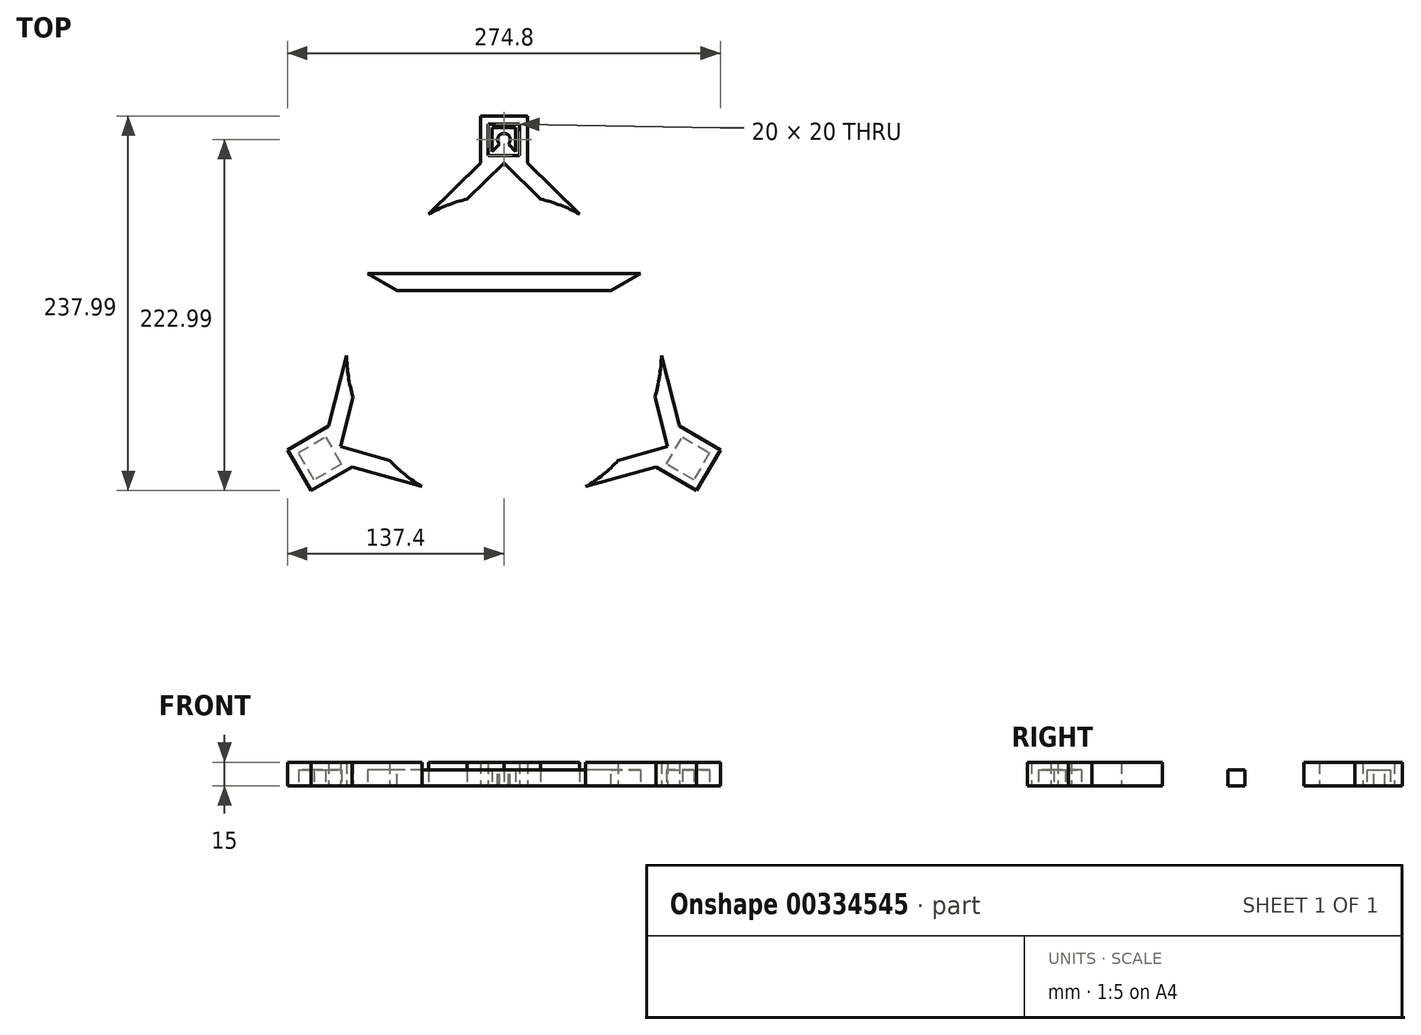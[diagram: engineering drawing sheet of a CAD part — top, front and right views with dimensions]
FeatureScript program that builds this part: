
annotation { "Feature Type Name" : "Feature", "Feature Type Description" : "" }
export const myFeature = defineFeature(function(context is Context, id is Id, definition is map)
    precondition{}
    {
        {
            var Q0;
            Q0=qCreatedBy(makeId("Top.planeOp"),FACE);
            var sketch = newSketch(context, id + "F0", { "sketchPlane" : qUnion([Q0])});
            skCircle(sketch, "E0", {"center": v(0, 0) * mm, "radius": 100 * mm});
            skLineSegment(sketch, "E1", {"start": v(0, 0) * mm, "end": v(0, -100) * mm});
            skLineSegment(sketch, "E2", {"start": v(0, 0) * mm, "end": v(86.6, 50) * mm});
            skLineSegment(sketch, "E3", {"start": v(0, 0) * mm, "end": v(-86.6, 50) * mm});
            skLineSegment(sketch, "E4", {"start": v(-86.6, 50) * mm, "end": v(0, -100) * mm});
            skLineSegment(sketch, "E5", {"start": v(0, -100) * mm, "end": v(86.6, 50) * mm});
            skLineSegment(sketch, "E6", {"start": v(86.6, 50) * mm, "end": v(-86.6, 50) * mm});
            skLineSegment(sketch, "E7", {"start": v(0, 0) * mm, "end": v(0, 125) * mm});
            skPoint(sketch, "E7.endSnap0", {"position": v(0, 50) * mm});
            skLineSegment(sketch, "E8", {"start": v(0, 0) * mm, "end": v(108.25, -62.5) * mm});
            skLineSegment(sketch, "E9", {"start": v(0, 0) * mm, "end": v(-108.25, -62.5) * mm});
            skLineSegment(sketch, "E10", {"start": v(-108.25, -62.5) * mm, "end": v(-113.25, -53.84) * mm});
            skLineSegment(sketch, "E11", {"start": v(-108.25, -62.5) * mm, "end": v(-103.25, -71.16) * mm});
            skLineSegment(sketch, "E12", {"start": v(-103.25, -71.16) * mm, "end": v(-120.57, -81.16) * mm});
            skLineSegment(sketch, "E13", {"start": v(-120.57, -81.16) * mm, "end": v(-130.57, -63.84) * mm});
            skLineSegment(sketch, "E14", {"start": v(-130.57, -63.84) * mm, "end": v(-113.25, -53.84) * mm});
            skLineSegment(sketch, "E15", {"start": v(0, 125) * mm, "end": v(10, 125) * mm});
            skLineSegment(sketch, "E16", {"start": v(10, 125) * mm, "end": v(10, 145) * mm});
            skLineSegment(sketch, "E17", {"start": v(10, 145) * mm, "end": v(-10, 145) * mm});
            skLineSegment(sketch, "E18", {"start": v(-10, 145) * mm, "end": v(-10, 125) * mm});
            skLineSegment(sketch, "E19", {"start": v(-10, 125) * mm, "end": v(0, 125) * mm});
            skLineSegment(sketch, "E20", {"start": v(108.25, -62.5) * mm, "end": v(113.25, -53.84) * mm});
            skLineSegment(sketch, "E21", {"start": v(113.25, -53.84) * mm, "end": v(130.57, -63.84) * mm});
            skLineSegment(sketch, "E22", {"start": v(130.57, -63.84) * mm, "end": v(120.57, -81.16) * mm});
            skLineSegment(sketch, "E23", {"start": v(120.57, -81.16) * mm, "end": v(103.25, -71.16) * mm});
            skLineSegment(sketch, "E24", {"start": v(103.25, -71.16) * mm, "end": v(108.25, -62.5) * mm});
            skLineSegment(sketch, "E25", {"start": v(-120.57, -81.16) * mm, "end": v(-113.25, -53.84) * mm});
            skLineSegment(sketch, "E26", {"start": v(-103.25, -71.16) * mm, "end": v(-130.57, -63.84) * mm});
            skLineSegment(sketch, "E27", {"start": v(113.25, -53.84) * mm, "end": v(120.57, -81.16) * mm});
            skLineSegment(sketch, "E28", {"start": v(103.25, -71.16) * mm, "end": v(130.57, -63.84) * mm});
            skLineSegment(sketch, "E29", {"start": v(-10, 145) * mm, "end": v(7.5, 127.5) * mm});
            skLineSegment(sketch, "E30", {"start": v(-7.5, 127.5) * mm, "end": v(10, 145) * mm});
            skLineSegment(sketch, "E31.bottom", {"start": v(15, 120) * mm, "end": v(-15, 120) * mm});
            skLineSegment(sketch, "E31.top", {"start": v(15, 150) * mm, "end": v(-15, 150) * mm});
            skLineSegment(sketch, "E31.left", {"start": v(15, 120) * mm, "end": v(15, 150) * mm});
            skLineSegment(sketch, "E31.right", {"start": v(-15, 120) * mm, "end": v(-15, 150) * mm});
            skPoint(sketch, "E31.middle", {"position": v(0, 135) * mm});
            skLineSegment(sketch, "E32", {"start": v(-15, 120) * mm, "end": v(-86.6, 50) * mm});
            skLineSegment(sketch, "E33", {"start": v(-86.6, 50) * mm, "end": v(-71.6, 50) * mm});
            skLineSegment(sketch, "E34", {"start": v(-71.6, 50) * mm, "end": v(0, 120) * mm});
            skLineSegment(sketch, "E35", {"start": v(86.6, 50) * mm, "end": v(71.6, 50) * mm});
            skLineSegment(sketch, "E36", {"start": v(71.6, 50) * mm, "end": v(0, 120) * mm});
            skLineSegment(sketch, "E37", {"start": v(15, 120) * mm, "end": v(86.6, 50) * mm});
            skLineSegment(sketch, "E38.bottom", {"start": v(-10, 125) * mm, "end": v(10, 125) * mm});
            skLineSegment(sketch, "E38.top", {"start": v(-10, 127.5) * mm, "end": v(10, 127.5) * mm});
            skLineSegment(sketch, "E38.left", {"start": v(-10, 125) * mm, "end": v(-10, 127.5) * mm});
            skLineSegment(sketch, "E38.right", {"start": v(10, 125) * mm, "end": v(10, 127.5) * mm});
            skLineSegment(sketch, "E39.bottom", {"start": v(7.5, 127.5) * mm, "end": v(-7.5, 127.5) * mm});
            skLineSegment(sketch, "E39.top", {"start": v(7.5, 142.5) * mm, "end": v(-7.5, 142.5) * mm});
            skLineSegment(sketch, "E39.left", {"start": v(7.5, 127.5) * mm, "end": v(7.5, 142.5) * mm});
            skLineSegment(sketch, "E39.right", {"start": v(-7.5, 127.5) * mm, "end": v(-7.5, 142.5) * mm});
            skSolve(sketch);
        }
        {
            var Q0;
            {var subQ5=sQuery(id+"F0.wireOp",EDGE,"E33");Q0=makeQuery(id+"F0.imprint","IMPRINT",FACE,{"disambiguationData":[TD([[makeQuery(id+"F0.imprint","IMPRINT",EDGE,{"derivedFrom":subQ5}),1.0]])]});}
            var Q1;
            {var subQ0=sQuery(id+"F0.wireOp",EDGE,"E32");var subQ1=sQuery(id+"F0.wireOp",EDGE,"E0");var subQ2=makeQuery(id+"F0.imprint","INTERSECT",VERTEX,{"derivedFrom":[subQ1,subQ0]});Q1=makeQuery(id+"F0.imprint","IMPRINT",FACE,{"disambiguationData":[TD([[makeQuery(id+"F0.imprint","IMPRINT",EDGE,{"disambiguationData":[TD([[subQ2,1.0]])],"derivedFrom":subQ1}),-1.0]])]});}
            var Q2;
            {var subQ0=sQuery(id+"F0.wireOp",EDGE,"E37");var subQ1=sQuery(id+"F0.wireOp",EDGE,"E0");var subQ2=makeQuery(id+"F0.imprint","INTERSECT",VERTEX,{"derivedFrom":[subQ1,subQ0]});Q2=makeQuery(id+"F0.imprint","IMPRINT",FACE,{"disambiguationData":[TD([[makeQuery(id+"F0.imprint","IMPRINT",EDGE,{"disambiguationData":[TD([[subQ2,-1.0]])],"derivedFrom":subQ1}),-1.0]])]});}
            var Q3;
            {var subQ5=sQuery(id+"F0.wireOp",EDGE,"E35");Q3=makeQuery(id+"F0.imprint","IMPRINT",FACE,{"disambiguationData":[TD([[makeQuery(id+"F0.imprint","IMPRINT",EDGE,{"derivedFrom":subQ5}),-1.0]])]});}
            var Q4;
            Q4=makeQuery(id+"F0.imprint","IMPRINT",FACE,{"disambiguationData":[TD([[makeQuery(id+"F0.imprint","IMPRINT",EDGE,{"derivedFrom":sQuery(id+"F0.wireOp",EDGE,"E15")}),-1.0]])]});
            var Q5;
            {var subQ0=sQuery(id+"F0.wireOp",EDGE,"E3");Q5=makeQuery(id+"F0.imprint","IMPRINT",FACE,{"disambiguationData":[TD([[makeQuery(id+"F0.imprint","IMPRINT",EDGE,{"derivedFrom":subQ0}),-1.0]])]});}
            var Q6;
            {var subQ0=sQuery(id+"F0.wireOp",EDGE,"E2");Q6=makeQuery(id+"F0.imprint","IMPRINT",FACE,{"disambiguationData":[TD([[makeQuery(id+"F0.imprint","IMPRINT",EDGE,{"derivedFrom":subQ0}),1.0]])]});}
            var Q7;
            Q7=makeQuery(id+"F0.imprint","IMPRINT",FACE,{"disambiguationData":[TD([[makeQuery(id+"F0.imprint","IMPRINT",EDGE,{"derivedFrom":sQuery(id+"F0.wireOp",EDGE,"E16")}),-1.0]])]});
            var Q8;
            {var subQ3=sQuery(id+"F0.wireOp",EDGE,"E38.left");Q8=makeQuery(id+"F0.imprint","IMPRINT",FACE,{"disambiguationData":[TD([[makeQuery(id+"F0.imprint","IMPRINT",EDGE,{"derivedFrom":subQ3}),-1.0]])]});}
            var Q9;
            {var subQ0=sQuery(id+"F0.wireOp",EDGE,"E39.right");Q9=makeQuery(id+"F0.imprint","IMPRINT",FACE,{"disambiguationData":[TD([[makeQuery(id+"F0.imprint","IMPRINT",EDGE,{"derivedFrom":subQ0}),-1.0]])]});}
            var Q10;
            {var subQ0=sQuery(id+"F0.wireOp",EDGE,"E39.bottom");Q10=makeQuery(id+"F0.imprint","IMPRINT",FACE,{"disambiguationData":[TD([[makeQuery(id+"F0.imprint","IMPRINT",EDGE,{"derivedFrom":subQ0}),-1.0]])]});}
            var Q11;
            {var subQ0=sQuery(id+"F0.wireOp",EDGE,"E39.top");Q11=makeQuery(id+"F0.imprint","IMPRINT",FACE,{"disambiguationData":[TD([[makeQuery(id+"F0.imprint","IMPRINT",EDGE,{"derivedFrom":subQ0}),1.0]])]});}
            var Q12;
            {var subQ0=sQuery(id+"F0.wireOp",EDGE,"E39.left");Q12=makeQuery(id+"F0.imprint","IMPRINT",FACE,{"disambiguationData":[TD([[makeQuery(id+"F0.imprint","IMPRINT",EDGE,{"derivedFrom":subQ0}),1.0]])]});}
            extrude(context, id + "F1", {"entities" : qUnion([Q0, Q1, Q2, Q3, Q4, Q5, Q6, Q7, Q8, Q9, Q10, Q11, Q12]), "depth" : 10 * mm});
        }
        {
            var Q0;
            Q0=makeQuery(id+"F1.opExtrude","CAP_FACE",FACE,{"disambiguationData":[OSD([sQuery(id+"F0.wireOp",EDGE,"E2"),sQuery(id+"F0.wireOp",EDGE,"E3"),sQuery(id+"F0.wireOp",EDGE,"E6"),sQuery(id+"F0.wireOp",EDGE,"E16"),sQuery(id+"F0.wireOp",EDGE,"E17"),sQuery(id+"F0.wireOp",EDGE,"E18"),sQuery(id+"F0.wireOp",EDGE,"E31.top"),sQuery(id+"F0.wireOp",EDGE,"E31.left"),sQuery(id+"F0.wireOp",EDGE,"E31.right"),sQuery(id+"F0.wireOp",EDGE,"E32"),sQuery(id+"F0.wireOp",EDGE,"E34"),sQuery(id+"F0.wireOp",EDGE,"E36"),sQuery(id+"F0.wireOp",EDGE,"E37"),sQuery(id+"F0.wireOp",EDGE,"E38.top"),sQuery(id+"F0.wireOp",EDGE,"E39.top"),sQuery(id+"F0.wireOp",EDGE,"E39.left"),sQuery(id+"F0.wireOp",EDGE,"E39.right")])],"isStart":false});
            var sketch = newSketch(context, id + "F2", { "sketchPlane" : qUnion([Q0])});
            skLineSegment(sketch, "E40.bottom", {"start": v(-7.5, 142.5) * mm, "end": v(7.5, 142.5) * mm});
            skLineSegment(sketch, "E40.top", {"start": v(-7.5, 127.5) * mm, "end": v(7.5, 127.5) * mm});
            skLineSegment(sketch, "E40.left", {"start": v(-7.5, 142.5) * mm, "end": v(-7.5, 127.5) * mm});
            skLineSegment(sketch, "E40.right", {"start": v(7.5, 142.5) * mm, "end": v(7.5, 127.5) * mm});
            skCircle(sketch, "E41", {"center": v(0, 135) * mm, "radius": 4 * mm});
            skPoint(sketch, "E41.centerSnap0", {"position": v(-7.5, 135) * mm});
            skSolve(sketch);
        }
        {
            var Q0;
            Q0=makeQuery(id+"F2.imprint","IMPRINT",FACE,{"disambiguationData":[TD([[makeQuery(id+"F2.imprint","IMPRINT",EDGE,{"derivedFrom":sQuery(id+"F2.wireOp",EDGE,"E41")}),1.0]])]});
            extrude(context, id + "F3", {"entities" : qUnion([Q0]), "operationType" : NewBodyOperationType.REMOVE, "oppositeDirection" : true, "depth" : 25 * mm});
        }
        {
            var Q0;
            Q0=makeQuery(id+"F1.opExtrude","SWEPT_BODY",BODY,{"disambiguationData":[OSD([sQuery(id+"F0.wireOp",EDGE,"E2"),sQuery(id+"F0.wireOp",EDGE,"E3"),sQuery(id+"F0.wireOp",EDGE,"E6"),sQuery(id+"F0.wireOp",EDGE,"E15"),sQuery(id+"F0.wireOp",EDGE,"E16"),sQuery(id+"F0.wireOp",EDGE,"E17"),sQuery(id+"F0.wireOp",EDGE,"E18"),sQuery(id+"F0.wireOp",EDGE,"E19"),sQuery(id+"F0.wireOp",EDGE,"E31.top"),sQuery(id+"F0.wireOp",EDGE,"E31.left"),sQuery(id+"F0.wireOp",EDGE,"E31.right"),sQuery(id+"F0.wireOp",EDGE,"E32"),sQuery(id+"F0.wireOp",EDGE,"E34"),sQuery(id+"F0.wireOp",EDGE,"E36"),sQuery(id+"F0.wireOp",EDGE,"E37")])]});
            var Q1;
            Q1=makeQuery(id+"F1.opExtrude","SWEPT_FACE",FACE,{"disambiguationData":[OSD([sQuery(id+"F0.wireOp",EDGE,"E3")])]});
            mirror(context, id + "F4", {"entities" : qUnion([Q0]), "mirrorPlane" : qUnion([Q1])});
        }
        {
            var Q0;
            Q0=makeQuery(id+"F1.opExtrude","SWEPT_BODY",BODY,{"disambiguationData":[OSD([sQuery(id+"F0.wireOp",EDGE,"E2"),sQuery(id+"F0.wireOp",EDGE,"E3"),sQuery(id+"F0.wireOp",EDGE,"E6"),sQuery(id+"F0.wireOp",EDGE,"E15"),sQuery(id+"F0.wireOp",EDGE,"E16"),sQuery(id+"F0.wireOp",EDGE,"E17"),sQuery(id+"F0.wireOp",EDGE,"E18"),sQuery(id+"F0.wireOp",EDGE,"E19"),sQuery(id+"F0.wireOp",EDGE,"E31.top"),sQuery(id+"F0.wireOp",EDGE,"E31.left"),sQuery(id+"F0.wireOp",EDGE,"E31.right"),sQuery(id+"F0.wireOp",EDGE,"E32"),sQuery(id+"F0.wireOp",EDGE,"E34"),sQuery(id+"F0.wireOp",EDGE,"E36"),sQuery(id+"F0.wireOp",EDGE,"E37")])]});
            var Q1;
            Q1=makeQuery(id+"F1.opExtrude","SWEPT_FACE",FACE,{"disambiguationData":[OSD([sQuery(id+"F0.wireOp",EDGE,"E2")])]});
            mirror(context, id + "F5", {"operationType" : NewBodyOperationType.ADD, "entities" : qUnion([Q0]), "mirrorPlane" : qUnion([Q1])});
        }
        {
            var Q0;
            {var subQ0=makeQuery(id+"F1.opExtrude","CAP_FACE",FACE,{"disambiguationData":[OSD([sQuery(id+"F0.wireOp",EDGE,"E2"),sQuery(id+"F0.wireOp",EDGE,"E3"),sQuery(id+"F0.wireOp",EDGE,"E6"),sQuery(id+"F0.wireOp",EDGE,"E15"),sQuery(id+"F0.wireOp",EDGE,"E16"),sQuery(id+"F0.wireOp",EDGE,"E17"),sQuery(id+"F0.wireOp",EDGE,"E18"),sQuery(id+"F0.wireOp",EDGE,"E19"),sQuery(id+"F0.wireOp",EDGE,"E31.top"),sQuery(id+"F0.wireOp",EDGE,"E31.left"),sQuery(id+"F0.wireOp",EDGE,"E31.right"),sQuery(id+"F0.wireOp",EDGE,"E32"),sQuery(id+"F0.wireOp",EDGE,"E34"),sQuery(id+"F0.wireOp",EDGE,"E36"),sQuery(id+"F0.wireOp",EDGE,"E37")])],"isStart":false});Q0=makeQuery(id+"F5.boolean.opBoolean","MERGE",FACE,{"derivedFrom":[subQ0,makeQuery(id+"F4.opPattern","COPY",FACE,{"derivedFrom":subQ0,"instanceName":"1"}),makeQuery(id+"F5.opPattern","COPY",FACE,{"derivedFrom":subQ0,"instanceName":"1"})]});}
            var sketch = newSketch(context, id + "F6", { "sketchPlane" : qUnion([Q0])});
            skLineSegment(sketch, "E42", {"start": v(-79.1, 37) * mm, "end": v(-71.6, 50) * mm});
            skLineSegment(sketch, "E43", {"start": v(-71.6, 50) * mm, "end": v(71.6, 50) * mm});
            skLineSegment(sketch, "E44", {"start": v(71.6, 50) * mm, "end": v(79.1, 37) * mm});
            skLineSegment(sketch, "E45", {"start": v(79.1, 37) * mm, "end": v(7.5, -87) * mm});
            skLineSegment(sketch, "E46", {"start": v(7.5, -87) * mm, "end": v(-7.5, -87) * mm});
            skLineSegment(sketch, "E47", {"start": v(-7.5, -87) * mm, "end": v(-79.1, 37) * mm});
            skLineSegment(sketch, "E48", {"start": v(0, -78.35) * mm, "end": v(67.85, 39.17) * mm});
            skLineSegment(sketch, "E49", {"start": v(67.85, 39.17) * mm, "end": v(-67.85, 39.17) * mm});
            skLineSegment(sketch, "E50", {"start": v(-67.85, 39.17) * mm, "end": v(0, -78.35) * mm});
            skLineSegment(sketch, "E51", {"start": v(0, -87) * mm, "end": v(0, -78.35) * mm});
            skLineSegment(sketch, "E52", {"start": v(75.35, 43.5) * mm, "end": v(67.85, 39.17) * mm});
            skLineSegment(sketch, "E53", {"start": v(-75.35, 43.5) * mm, "end": v(-67.85, 39.17) * mm});
            skSolve(sketch);
        }
        {
            var Q0;
            Q0=makeQuery(id+"F6.imprint","IMPRINT",FACE,{"disambiguationData":[TD([[makeQuery(id+"F6.imprint","IMPRINT",EDGE,{"derivedFrom":sQuery(id+"F6.wireOp",EDGE,"E48")}),1.0]])]});
            extrude(context, id + "F7", {"entities" : qUnion([Q0]), "operationType" : NewBodyOperationType.REMOVE, "oppositeDirection" : true, "depth" : 25 * mm});
        }
        {
            var Q0;
            {var subQ0=makeQuery(id+"F1.opExtrude","CAP_FACE",FACE,{"disambiguationData":[OSD([sQuery(id+"F0.wireOp",EDGE,"E2"),sQuery(id+"F0.wireOp",EDGE,"E3"),sQuery(id+"F0.wireOp",EDGE,"E6"),sQuery(id+"F0.wireOp",EDGE,"E15"),sQuery(id+"F0.wireOp",EDGE,"E16"),sQuery(id+"F0.wireOp",EDGE,"E17"),sQuery(id+"F0.wireOp",EDGE,"E18"),sQuery(id+"F0.wireOp",EDGE,"E19"),sQuery(id+"F0.wireOp",EDGE,"E31.top"),sQuery(id+"F0.wireOp",EDGE,"E31.left"),sQuery(id+"F0.wireOp",EDGE,"E31.right"),sQuery(id+"F0.wireOp",EDGE,"E32"),sQuery(id+"F0.wireOp",EDGE,"E34"),sQuery(id+"F0.wireOp",EDGE,"E36"),sQuery(id+"F0.wireOp",EDGE,"E37")])],"isStart":false});Q0=makeQuery(id+"F5.boolean.opBoolean","MERGE",FACE,{"derivedFrom":[subQ0,makeQuery(id+"F4.opPattern","COPY",FACE,{"derivedFrom":subQ0,"instanceName":"1"}),makeQuery(id+"F5.opPattern","COPY",FACE,{"derivedFrom":subQ0,"instanceName":"1"})]});}
            var sketch = newSketch(context, id + "F8", { "sketchPlane" : qUnion([Q0])});
            skLineSegment(sketch, "E54", {"start": v(-15, 150) * mm, "end": v(-15, 120) * mm});
            skLineSegment(sketch, "E55", {"start": v(-15, 120) * mm, "end": v(15, 120) * mm});
            skLineSegment(sketch, "E56", {"start": v(15, 120) * mm, "end": v(15, 150) * mm});
            skLineSegment(sketch, "E57", {"start": v(15, 150) * mm, "end": v(-15, 150) * mm});
            skLineSegment(sketch, "E58", {"start": v(-111.42, -47) * mm, "end": v(-96.42, -73) * mm});
            skLineSegment(sketch, "E59", {"start": v(-96.42, -73) * mm, "end": v(-122.4, -88) * mm});
            skLineSegment(sketch, "E60", {"start": v(-122.4, -88) * mm, "end": v(-137.4, -62) * mm});
            skLineSegment(sketch, "E61", {"start": v(-137.4, -62) * mm, "end": v(-111.42, -47) * mm});
            skLineSegment(sketch, "E62", {"start": v(111.42, -47) * mm, "end": v(96.42, -73) * mm});
            skLineSegment(sketch, "E63", {"start": v(96.42, -73) * mm, "end": v(122.4, -88) * mm});
            skLineSegment(sketch, "E64", {"start": v(122.4, -88) * mm, "end": v(137.4, -62) * mm});
            skLineSegment(sketch, "E65", {"start": v(137.4, -62) * mm, "end": v(111.42, -47) * mm});
            skCircle(sketch, "E66", {"center": v(0, 0) * mm, "radius": 100 * mm});
            skLineSegment(sketch, "E67", {"start": v(-99.97, -2.26) * mm, "end": v(-111.42, -47) * mm});
            skLineSegment(sketch, "E68", {"start": v(-96.42, -73) * mm, "end": v(-51.95, -85.45) * mm});
            skLineSegment(sketch, "E69", {"start": v(96.42, -73) * mm, "end": v(51.95, -85.45) * mm});
            skLineSegment(sketch, "E70", {"start": v(111.42, -47) * mm, "end": v(99.97, -2.26) * mm});
            skLineSegment(sketch, "E71", {"start": v(15, 120) * mm, "end": v(48.03, 87.71) * mm});
            skLineSegment(sketch, "E72", {"start": v(-15, 120) * mm, "end": v(-48.03, 87.71) * mm});
            skLineSegment(sketch, "E73", {"start": v(-103.92, -60) * mm, "end": v(-95.46, -29.79) * mm});
            skLineSegment(sketch, "E74", {"start": v(-103.92, -60) * mm, "end": v(-72.6, -68.78) * mm});
            skLineSegment(sketch, "E75", {"start": v(103.92, -60) * mm, "end": v(72.6, -68.78) * mm});
            skLineSegment(sketch, "E76", {"start": v(103.92, -60) * mm, "end": v(95.86, -28.48) * mm});
            skLineSegment(sketch, "E77", {"start": v(0, 120) * mm, "end": v(23.26, 97.26) * mm});
            skLineSegment(sketch, "E78", {"start": v(0, 120) * mm, "end": v(-23.26, 97.26) * mm});
            skSolve(sketch);
        }
        {
            var Q0;
            {var subQ0=sQuery(id+"F8.wireOp",EDGE,"E72");Q0=makeQuery(id+"F8.imprint","IMPRINT",FACE,{"disambiguationData":[TD([[makeQuery(id+"F8.imprint","IMPRINT",EDGE,{"derivedFrom":subQ0}),1.0]])]});}
            var Q1;
            {var subQ0=sQuery(id+"F8.wireOp",EDGE,"E71");Q1=makeQuery(id+"F8.imprint","IMPRINT",FACE,{"disambiguationData":[TD([[makeQuery(id+"F8.imprint","IMPRINT",EDGE,{"derivedFrom":subQ0}),-1.0]])]});}
            var Q2;
            {var subQ3=sQuery(id+"F8.wireOp",EDGE,"E54");Q2=makeQuery(id+"F8.imprint","IMPRINT",FACE,{"disambiguationData":[TD([[makeQuery(id+"F8.imprint","IMPRINT",EDGE,{"derivedFrom":subQ3}),-1.0]])]});}
            var Q3;
            {var subQ0=sQuery(id+"F8.wireOp",EDGE,"E63");Q3=makeQuery(id+"F8.imprint","IMPRINT",FACE,{"disambiguationData":[TD([[makeQuery(id+"F8.imprint","IMPRINT",EDGE,{"derivedFrom":subQ0}),1.0]])]});}
            var Q4;
            {var subQ0=sQuery(id+"F8.wireOp",EDGE,"E70");Q4=makeQuery(id+"F8.imprint","IMPRINT",FACE,{"disambiguationData":[TD([[makeQuery(id+"F8.imprint","IMPRINT",EDGE,{"derivedFrom":subQ0}),1.0]])]});}
            var Q5;
            {var subQ0=sQuery(id+"F8.wireOp",EDGE,"E69");Q5=makeQuery(id+"F8.imprint","IMPRINT",FACE,{"disambiguationData":[TD([[makeQuery(id+"F8.imprint","IMPRINT",EDGE,{"derivedFrom":subQ0}),-1.0]])]});}
            var Q6;
            {var subQ0=sQuery(id+"F8.wireOp",EDGE,"E59");Q6=makeQuery(id+"F8.imprint","IMPRINT",FACE,{"disambiguationData":[TD([[makeQuery(id+"F8.imprint","IMPRINT",EDGE,{"derivedFrom":subQ0}),-1.0]])]});}
            var Q7;
            {var subQ0=sQuery(id+"F8.wireOp",EDGE,"E67");Q7=makeQuery(id+"F8.imprint","IMPRINT",FACE,{"disambiguationData":[TD([[makeQuery(id+"F8.imprint","IMPRINT",EDGE,{"derivedFrom":subQ0}),-1.0]])]});}
            var Q8;
            {var subQ0=sQuery(id+"F8.wireOp",EDGE,"E68");Q8=makeQuery(id+"F8.imprint","IMPRINT",FACE,{"disambiguationData":[TD([[makeQuery(id+"F8.imprint","IMPRINT",EDGE,{"derivedFrom":subQ0}),1.0]])]});}
            extrude(context, id + "F9", {"entities" : qUnion([Q0, Q1, Q2, Q3, Q4, Q5, Q6, Q7, Q8]), "operationType" : NewBodyOperationType.ADD, "depth" : 5 * mm});
        }
        {
            var Q0;
            {var subQ0=makeQuery(id+"F1.opExtrude","CAP_FACE",FACE,{"disambiguationData":[OSD([sQuery(id+"F0.wireOp",EDGE,"E2"),sQuery(id+"F0.wireOp",EDGE,"E3"),sQuery(id+"F0.wireOp",EDGE,"E6"),sQuery(id+"F0.wireOp",EDGE,"E15"),sQuery(id+"F0.wireOp",EDGE,"E16"),sQuery(id+"F0.wireOp",EDGE,"E17"),sQuery(id+"F0.wireOp",EDGE,"E18"),sQuery(id+"F0.wireOp",EDGE,"E19"),sQuery(id+"F0.wireOp",EDGE,"E31.top"),sQuery(id+"F0.wireOp",EDGE,"E31.left"),sQuery(id+"F0.wireOp",EDGE,"E31.right"),sQuery(id+"F0.wireOp",EDGE,"E32"),sQuery(id+"F0.wireOp",EDGE,"E34"),sQuery(id+"F0.wireOp",EDGE,"E36"),sQuery(id+"F0.wireOp",EDGE,"E37")])],"isStart":false});Q0=makeQuery(id+"F5.boolean.opBoolean","MERGE",FACE,{"derivedFrom":[subQ0,makeQuery(id+"F4.opPattern","COPY",FACE,{"derivedFrom":subQ0,"instanceName":"1"}),makeQuery(id+"F5.opPattern","COPY",FACE,{"derivedFrom":subQ0,"instanceName":"1"})]});}
            extrude(context, id + "F10", {"entities" : qUnion([Q0]), "operationType" : NewBodyOperationType.ADD, "depth" : 5 * mm});
        }
    });
